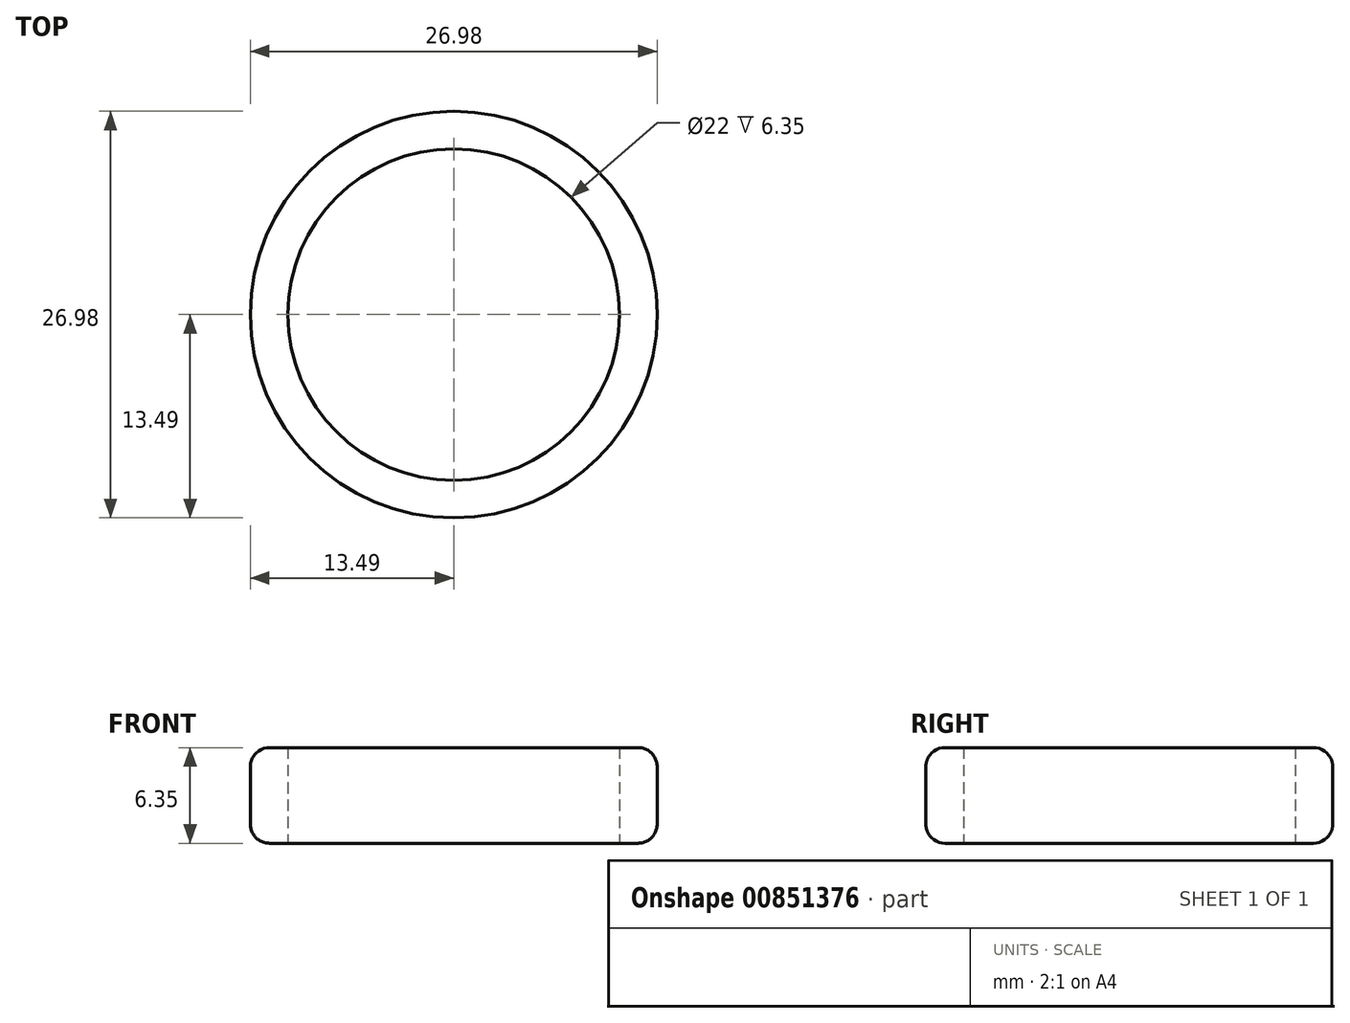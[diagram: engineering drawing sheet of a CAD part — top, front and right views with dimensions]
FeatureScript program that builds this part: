
annotation { "Feature Type Name" : "Feature", "Feature Type Description" : "" }
export const myFeature = defineFeature(function(context is Context, id is Id, definition is map)
    precondition{}
    {
        {
            var Q0;
            Q0=qCreatedBy(makeId("Top.planeOp"),FACE);
            var sketch = newSketch(context, id + "F0", { "sketchPlane" : qUnion([Q0])});
            skCircle(sketch, "E0", {"center": v(0, 0) * mm, "radius": 11 * mm});
            skCircle(sketch, "E1", {"center": v(0, 0) * mm, "radius": 13.5 * mm});
            skSolve(sketch);
        }
        {
            var Q0;
            Q0=makeQuery(id+"F0.imprint","IMPRINT",FACE,{"disambiguationData":[TD([[makeQuery(id+"F0.imprint","IMPRINT",EDGE,{"derivedFrom":sQuery(id+"F0.wireOp",EDGE,"E0")}),-1.0]])]});
            extrude(context, id + "F1", {"entities" : qUnion([Q0]), "depth" : 6.35 * mm, "offsetDistance" : 25.4 * mm});
        }
        {
            var Q0;
            Q0=makeQuery(id+"F1.opExtrude","CAP_EDGE",EDGE,{"disambiguationData":[OSD([sQuery(id+"F0.wireOp",EDGE,"E1")])],"isStart":true});
            fillet(context, id + "F2", {"entities" : qUnion([Q0]), "radius" : 1.27 * mm, "tangentPropagation" : true, "allowEdgeOverflow" : false});
        }
        {
            var Q0;
            Q0=makeQuery(id+"F1.opExtrude","CAP_EDGE",EDGE,{"disambiguationData":[OSD([sQuery(id+"F0.wireOp",EDGE,"E1")])],"isStart":false});
            fillet(context, id + "F3", {"entities" : qUnion([Q0]), "radius" : 1.27 * mm, "tangentPropagation" : true, "allowEdgeOverflow" : false});
        }
    });
